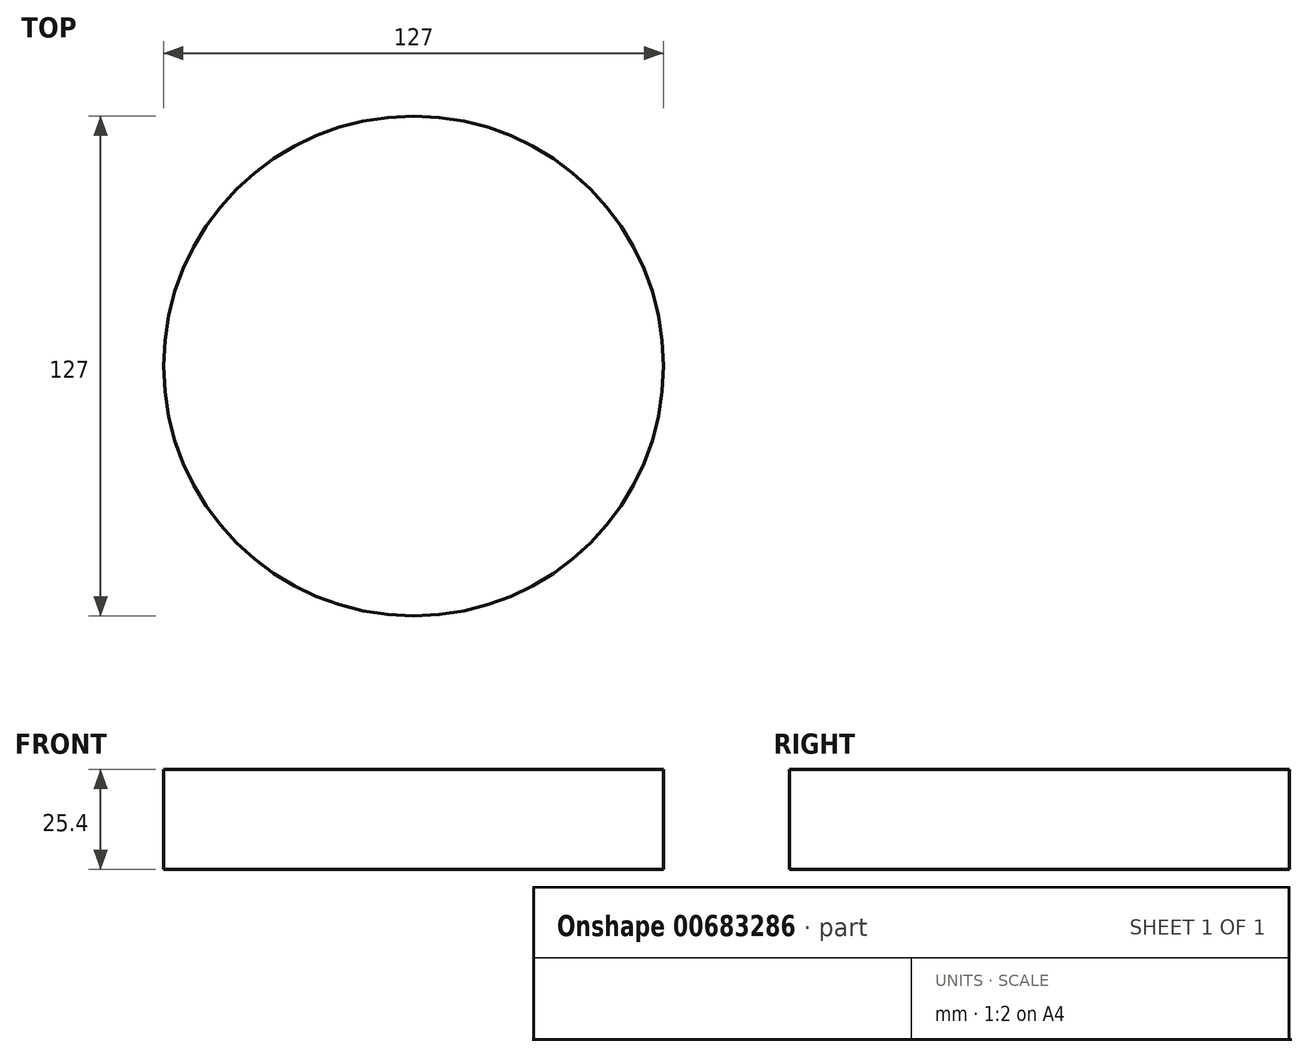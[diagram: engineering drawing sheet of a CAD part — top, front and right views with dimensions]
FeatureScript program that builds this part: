
annotation { "Feature Type Name" : "Feature", "Feature Type Description" : "" }
export const myFeature = defineFeature(function(context is Context, id is Id, definition is map)
    precondition{}
    {
        {
            var Q0;
            Q0=qCreatedBy(makeId("Top.planeOp"),FACE);
            var sketch = newSketch(context, id + "F0", { "sketchPlane" : qUnion([Q0])});
            skCircle(sketch, "E0", {"center": v(0, 0) * mm, "radius": 63.5 * mm});
            skSolve(sketch);
        }
        {
            var Q0;
            Q0 = qSketchRegion(id + "F0", true);
            extrude(context, id + "F1", {"entities" : qUnion([Q0]), "depth" : 25.4 * mm, "offsetDistance" : 25.4 * mm});
        }
    });
